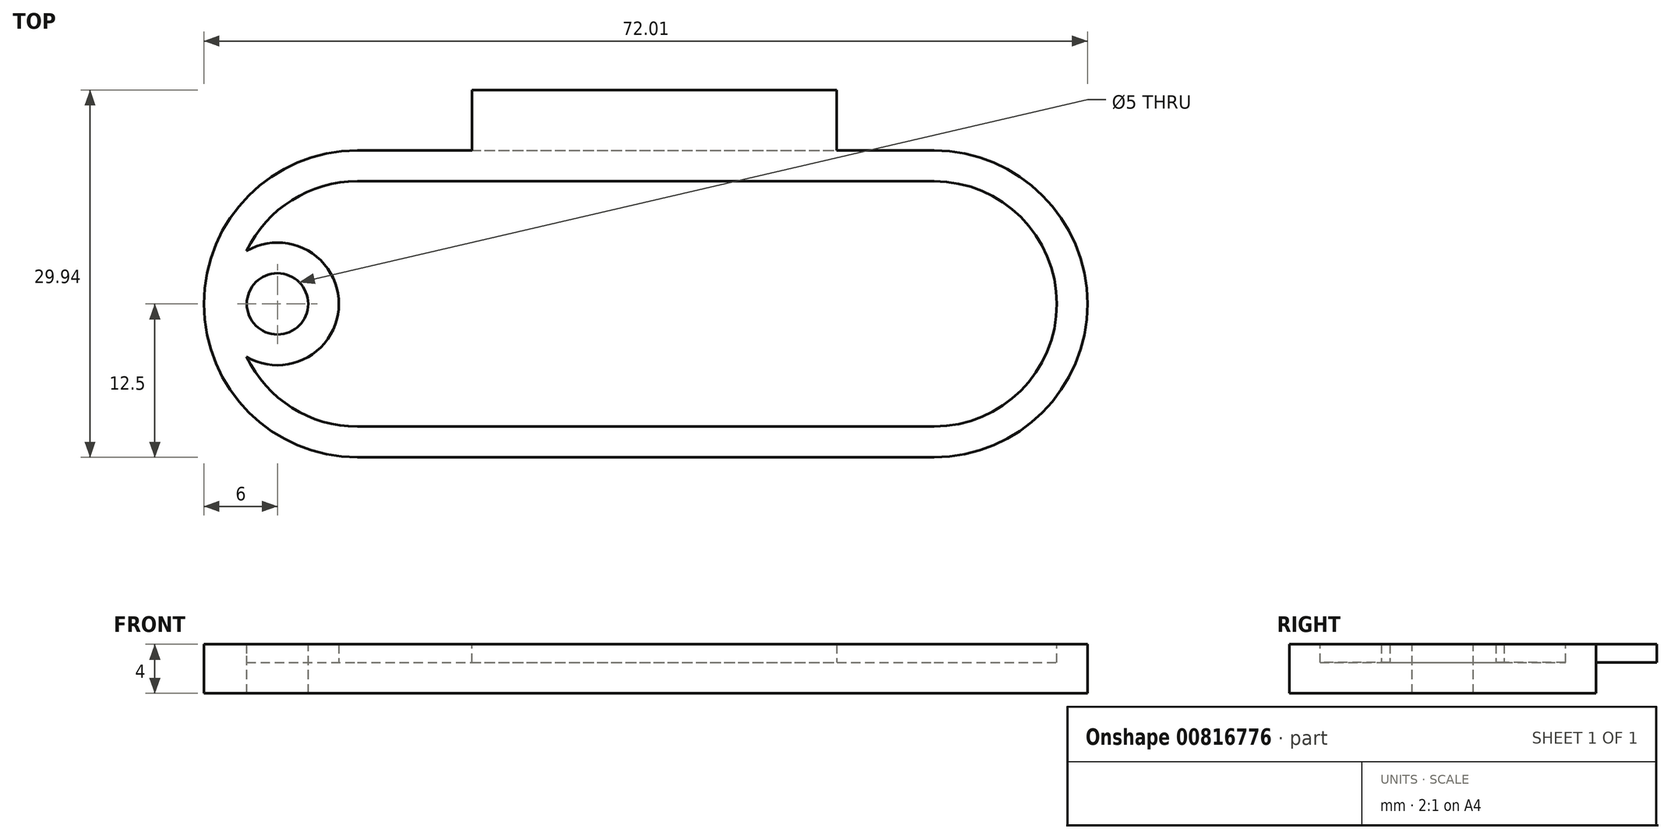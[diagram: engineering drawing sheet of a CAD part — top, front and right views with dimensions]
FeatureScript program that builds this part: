
annotation { "Feature Type Name" : "Feature", "Feature Type Description" : "" }
export const myFeature = defineFeature(function(context is Context, id is Id, definition is map)
    precondition{}
    {
        {
            var Q0;
            Q0=qCreatedBy(makeId("Top.planeOp"),FACE);
            var sketch = newSketch(context, id + "F0", { "sketchPlane" : qUnion([Q0])});
            skLineSegment(sketch, "E0.bottom", {"start": v(12.5, 0) * mm, "end": v(59.5, 0) * mm});
            skLineSegment(sketch, "E0.top", {"start": v(12.5, 25) * mm, "end": v(59.5, 25) * mm});
            skArc(sketch, "E1", {"start": v(12.5, 25) * mm, "mid": v(0, 12.5) * mm, "end": v(12.5, 0) * mm});
            skPoint(sketch, "E1.centerSnap0", {"position": v(0, 12.5) * mm});
            skArc(sketch, "E2", {"start": v(59.5, 0) * mm, "mid": v(72, 12.5) * mm, "end": v(59.5, 25) * mm});
            skPoint(sketch, "E2.centerSnap0", {"position": v(75, 12.5) * mm});
            skPoint(sketch, "E3.orphan", {"position": v(0, 25) * mm});
            skPoint(sketch, "E0.left.start.orphan", {"position": v(0, 0) * mm});
            skPoint(sketch, "E4.orphan", {"position": v(75, 25) * mm});
            skPoint(sketch, "E5.orphan", {"position": v(75, 0) * mm});
            skSolve(sketch);
        }
        {
            var Q0;
            Q0=makeQuery(id+"F0.imprint","IMPRINT",FACE,{"disambiguationData":[TD([[makeQuery(id+"F0.imprint","IMPRINT",EDGE,{"derivedFrom":sQuery(id+"F0.wireOp",EDGE,"E0.bottom")}),1.0]])]});
            extrude(context, id + "F1", {"entities" : qUnion([Q0]), "depth" : 4 * mm, "offsetDistance" : 25 * mm});
        }
        {
            var Q0;
            Q0=makeQuery(id+"F1.opExtrude","CAP_FACE",FACE,{"disambiguationData":[OSD([sQuery(id+"F0.wireOp",EDGE,"E0.bottom"),sQuery(id+"F0.wireOp",EDGE,"E0.top"),sQuery(id+"F0.wireOp",EDGE,"E1"),sQuery(id+"F0.wireOp",EDGE,"E2")])],"isStart":false});
            var sketch = newSketch(context, id + "F2", { "sketchPlane" : qUnion([Q0])});
            skArc(sketch, "E6", {"start": v(12.5, 22.5) * mm, "mid": v(2.5, 12.5) * mm, "end": v(12.5, 2.5) * mm});
            skArc(sketch, "E7", {"start": v(59.5, 2.5) * mm, "mid": v(69.5, 12.5) * mm, "end": v(59.5, 22.5) * mm});
            skLineSegment(sketch, "E8", {"start": v(12.5, 22.5) * mm, "end": v(59.5, 22.5) * mm});
            skLineSegment(sketch, "E9", {"start": v(12.5, 2.5) * mm, "end": v(59.5, 2.5) * mm});
            skSolve(sketch);
        }
        {
            var Q0;
            Q0=makeQuery(id+"F2.imprint","IMPRINT",FACE,{"disambiguationData":[TD([[makeQuery(id+"F2.imprint","IMPRINT",EDGE,{"derivedFrom":sQuery(id+"F2.wireOp",EDGE,"E6")}),1.0]])]});
            extrude(context, id + "F3", {"entities" : qUnion([Q0]), "operationType" : NewBodyOperationType.REMOVE, "oppositeDirection" : true, "depth" : 1.5 * mm, "offsetDistance" : 25 * mm});
        }
        {
            var Q0;
            Q0=makeQuery(id+"F3.boolean.opBoolean","COPY",FACE,{"derivedFrom":makeQuery(id+"F3.opExtrude","CAP_FACE",FACE,{"disambiguationData":[OSD([sQuery(id+"F2.wireOp",EDGE,"E6"),sQuery(id+"F2.wireOp",EDGE,"E7"),sQuery(id+"F2.wireOp",EDGE,"E8"),sQuery(id+"F2.wireOp",EDGE,"E9")])],"isStart":false})});
            var sketch = newSketch(context, id + "F4", { "sketchPlane" : qUnion([Q0])});
            skCircle(sketch, "E10", {"center": v(6, 12.5) * mm, "radius": 5 * mm});
            skPoint(sketch, "E10.centerSnap0", {"position": v(2.5, 12.5) * mm});
            skSolve(sketch);
        }
        {
            var Q0;
            {var subQ0=sQuery(id+"F4.wireOp",EDGE,"E10");var subQ1=makeQuery(id+"F3.boolean.opBoolean","COPY",EDGE,{"derivedFrom":makeQuery(id+"F3.opExtrude","CAP_EDGE",EDGE,{"disambiguationData":[OSD([sQuery(id+"F2.wireOp",EDGE,"E6")])],"isStart":false})});var subQ2=makeQuery(id+"F4.imprint","INTERSECT",VERTEX,{"disambiguationData":[OD(0.0)],"derivedFrom":[subQ1,subQ0]});Q0=makeQuery(id+"F4.imprint","IMPRINT",FACE,{"disambiguationData":[TD([[makeQuery(id+"F4.imprint","IMPRINT",EDGE,{"disambiguationData":[TD([[subQ2,1.0]])],"derivedFrom":subQ0}),1.0]])]});}
            extrude(context, id + "F5", {"entities" : qUnion([Q0]), "operationType" : NewBodyOperationType.ADD, "depth" : 1.5 * mm, "offsetDistance" : 25 * mm});
        }
        {
            var Q0;
            Q0=makeQuery(id+"F5.boolean.opBoolean","MERGE",FACE,{"derivedFrom":[makeQuery(id+"F1.opExtrude","CAP_FACE",FACE,{"disambiguationData":[OSD([sQuery(id+"F0.wireOp",EDGE,"E0.bottom"),sQuery(id+"F0.wireOp",EDGE,"E0.top"),sQuery(id+"F0.wireOp",EDGE,"E1"),sQuery(id+"F0.wireOp",EDGE,"E2")])],"isStart":false}),makeQuery(id+"F5.opExtrude","CAP_FACE",FACE,{"disambiguationData":[OSD([sQuery(id+"F2.wireOp",EDGE,"E6"),sQuery(id+"F4.wireOp",EDGE,"E10")])],"isStart":false})]});
            var sketch = newSketch(context, id + "F6", { "sketchPlane" : qUnion([Q0])});
            skCircle(sketch, "E11", {"center": v(6, 12.5) * mm, "radius": 2.5 * mm});
            skSolve(sketch);
        }
        {
            var Q0;
            Q0=makeQuery(id+"F6.imprint","IMPRINT",FACE,{"disambiguationData":[TD([[makeQuery(id+"F6.imprint","IMPRINT",EDGE,{"derivedFrom":sQuery(id+"F6.wireOp",EDGE,"E11")}),1.0]])]});
            extrude(context, id + "F7", {"entities" : qUnion([Q0]), "operationType" : NewBodyOperationType.REMOVE, "oppositeDirection" : true, "depth" : 25 * mm, "offsetDistance" : 25 * mm});
        }
        {
            var Q0;
            Q0=makeQuery(id+"F3.boolean.opBoolean","COPY",FACE,{"derivedFrom":makeQuery(id+"F3.opExtrude","CAP_FACE",FACE,{"disambiguationData":[OSD([sQuery(id+"F2.wireOp",EDGE,"E6"),sQuery(id+"F2.wireOp",EDGE,"E7"),sQuery(id+"F2.wireOp",EDGE,"E8"),sQuery(id+"F2.wireOp",EDGE,"E9")])],"isStart":false})});
            var sketch = newSketch(context, id + "F8", { "sketchPlane" : qUnion([Q0])});
            skText(sketch, "E12", { "text": "1", "fontName": "OpenSans-Bold.ttf"});
            const initialGuessF8  = {"E12": [0.05158, 0.01273, 0, 1, 0.03]};
            skSetInitialGuess(sketch, initialGuessF8);
            skSolve(sketch);
        }
        {
            var Q0;
            Q0=makeQuery(id+"F8.imprint","IMPRINT",FACE,{"disambiguationData":[TD([[makeQuery(id+"F8.imprint","IMPRINT",EDGE,{"derivedFrom":sQuery(id+"F8.wireOp",EDGE,"E12.sketch_text.stroke-0")}),-1.0]])]});
            extrude(context, id + "F9", {"entities" : qUnion([Q0]), "operationType" : NewBodyOperationType.ADD, "depth" : 1.5 * mm, "offsetDistance" : 25 * mm});
        }
    });
